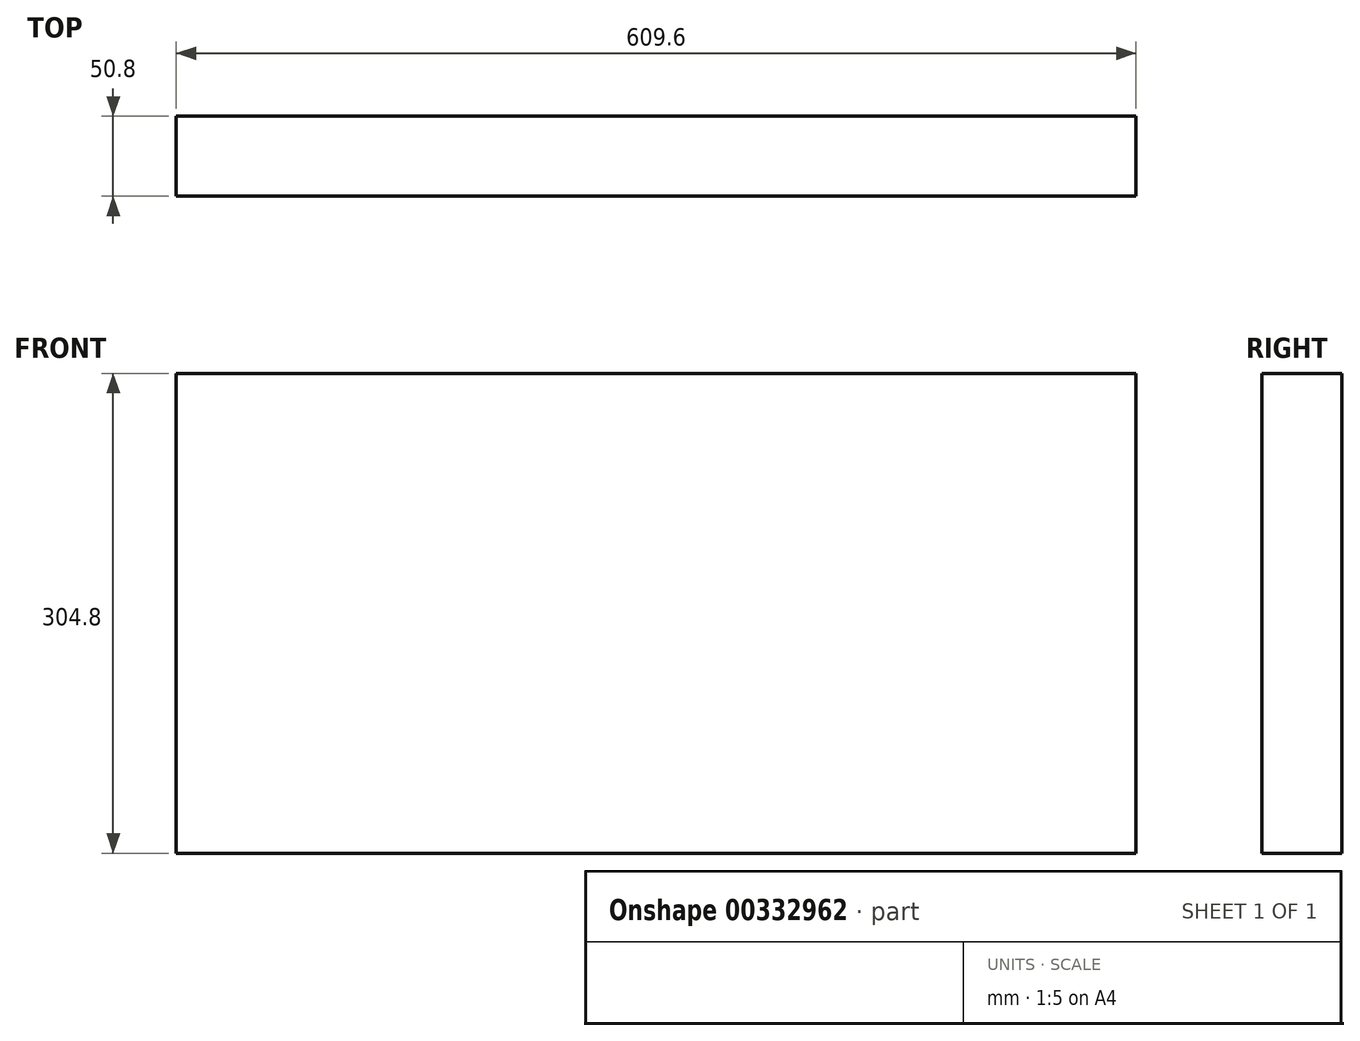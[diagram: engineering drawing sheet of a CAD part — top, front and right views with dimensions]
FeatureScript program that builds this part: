
annotation { "Feature Type Name" : "Feature", "Feature Type Description" : "" }
export const myFeature = defineFeature(function(context is Context, id is Id, definition is map)
    precondition{}
    {
        {
            var Q0;
            Q0=qCreatedBy(makeId("Front.planeOp"),FACE);
            var sketch = newSketch(context, id + "F0", { "sketchPlane" : qUnion([Q0])});
            skLineSegment(sketch, "E0.bottom", {"start": v(304.8, -152.4) * mm, "end": v(-304.8, -152.4) * mm});
            skLineSegment(sketch, "E0.top", {"start": v(304.8, 152.4) * mm, "end": v(-304.8, 152.4) * mm});
            skLineSegment(sketch, "E0.left", {"start": v(304.8, -152.4) * mm, "end": v(304.8, 152.4) * mm});
            skLineSegment(sketch, "E0.right", {"start": v(-304.8, -152.4) * mm, "end": v(-304.8, 152.4) * mm});
            skPoint(sketch, "E0.middle", {"position": v(0, 0) * mm});
            skSolve(sketch);
        }
        {
            var Q0;
            Q0 = qSketchRegion(id + "F0", true);
            extrude(context, id + "F1", {"entities" : qUnion([Q0]), "depth" : 50.8 * mm});
        }
    });
